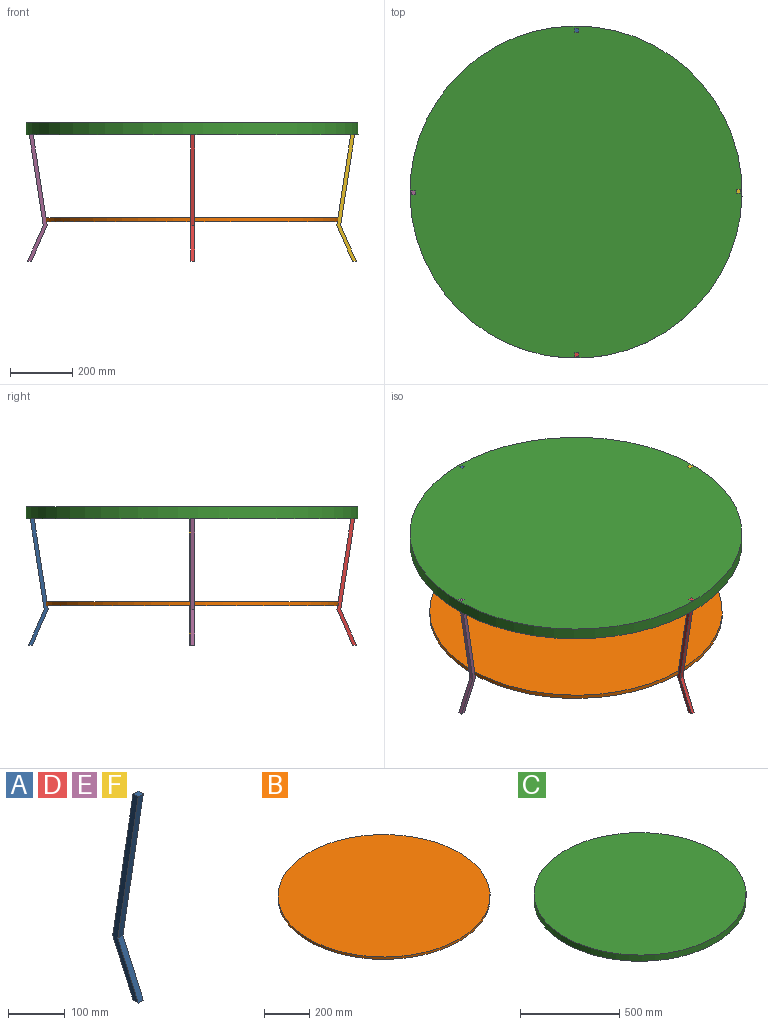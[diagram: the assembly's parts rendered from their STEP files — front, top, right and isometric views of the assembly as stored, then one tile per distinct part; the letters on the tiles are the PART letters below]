
ASSEMBLY  parts=6 mates=4
PART A: 8 faces, bbox 12.7x63.5x444.5 mm
  f0: plane 12.7x12.7mm, normal (0,0,1), area 161.3mm2, adj f1,f5,f6,f7
  f1: plane 330.2x50.8mm, normal (0,-0.99,-0.15), area 4242.9mm2, adj f0,f2,f6,f7
  f2: plane 114.3x50.8mm, normal (0,-0.91,0.41), area 1588.5mm2, adj f1,f3,f6,f7
  f3: plane 12.7x12.7mm, normal (0,0,-1), area 161.3mm2, adj f2,f4,f6,f7
  f4: plane 114.3x50.8mm, normal (0,0.91,-0.41), area 1588.5mm2, adj f3,f5,f6,f7
  f5: plane 330.2x50.8mm, normal (0,0.99,0.15), area 4242.9mm2, adj f0,f4,f6,f7
  f6: plane 444.5x63.5mm, normal (1,0,0), area 5645.2mm2, adj f0,f1,f2,f3,f4,f5
  f7: plane 444.5x63.5mm, normal (-1,0,0), area 5645.2mm2, adj f0,f1,f2,f3,f4,f5
PART B: 3 faces, bbox 939.8x939.8x12.7 mm
  f0: cylinder r=469.9mm len=939.8mm, axis (0,0,-1), area 37496.4mm2, adj f1,f2
  f1: plane 939.8x939.8mm, normal (0,0,1), area 693682.5mm2, adj f0
  f2: plane 939.8x939.8mm, normal (0,0,-1), area 693682.5mm2, adj f0
PART C: 3 faces, bbox 1066.8x1066.8x38.1 mm
  f0: cylinder r=533.4mm len=1066.8mm, axis (0,0,-1), area 127690.3mm2, adj f1,f2
  f1: plane 1066.8x1066.8mm, normal (0,0,1), area 893832mm2, adj f0
  f2: plane 1066.8x1066.8mm, normal (0,0,-1), area 893832mm2, adj f0
PART D: same geometry as A
PART E: same geometry as A
PART F: same geometry as A
PLACE A rot(axis=(0,0,1),180deg) t=(-248.22,-698.65,-264.03)mm
PLACE B rot(axis=(0,0,-1),55deg) t=(-250.76,-691.03,-475.82)mm
PLACE C rot(axis=(0,0,1),33.9deg) t=(-250.76,-691.03,-196.42)mm
PLACE D t=(-248.22,-685.95,-264.03)mm
PLACE E rot(axis=(0,0,-1),90deg) t=(-245.68,-693.57,-264.03)mm
PLACE F rot(axis=(0,0,1),90deg) t=(-255.84,-688.49,-264.03)mm
MATE planar C.f0 <-> B.f0  axis (0,0,1) through (-250.76,-691.03,-158.32)mm
MATE planar D.f0 <-> C.f0  axis (0,0,1) through (-248.22,-1213,-158.32)mm
MATE fastened A.f3 <-> D.f3  axis (0,0,-1) through (-248.22,-171.6,-602.82)mm
MATE cylindrical C.f0 <-> B.f0  axis (0,0,1) through (-250.76,-691.03,-158.32)mm
